# Revit family: r2018_videomax_videoserver_stoechnogo_ispolneniya
name_source: partatom
category: Устройства связи
revit_build: Autodesk Revit 2018 (Build: 20181011_1500(x64)
units: mm (PartAtom-declared; Revit-internal decimal feet)

## family parameters
Общий = Нет
Основа = Грань
При загрузке вырезать с полостями = Нет
Размер круглого соединителя = Использовать диаметр
Сохранять ориентацию аннотаций = Да
Тип детали = Нормальный
Точка расчета площади = Нет

## types (12) — shared parameters
ADSK_Версия Revit = 2018
ADSK_Версия семейства = v3
ADSK_Единица измерения = шт.
ADSK_Завод-изготовитель = ООО «Видеомакс»
ADSK_Код изделия = ТУ 26.20.15-002-37165186-2020
ADSK_Количество = 1
ADSK_Коэффициент мощности = 0.96
ADSK_Марка = VIDEOMAX-IP
ADSK_Напряжение = 230 В
ADSK_Номинальная мощность = 0 В·А
ADSK_Ток = 0 А
Material = Черный
URL = https://www.videomax-server.ru
Изготовитель = ООО «Видеомакс»
Количество интерфейсов Gigabit LAN, шт = 2
zero-valued in all types: ADSK_Масса, Количество IP-камер. шт, Количество интерфейсов 10 Gigabit LAN, шт, Максимальная мощность БП, Вт, Максимальная потребляемая мощность Вт, Максимальное тепловыделение, BTU/h, Отметка по умолчанию, Стоимость

## per-type parameters (varying)
- 19” 2U (2S): 19” 1U (1DT)=Нет; 19” 1U (1DTS)=Нет; 19” 2U (2ET)=Нет; 19” 2U (2ETS)=Нет; 19” 2U (2F)=Нет; 19” 2U (2S)=Да; 19” 3U (3ET)=Нет; 19” 3U (3ETS)=Нет; 19” 3U (3S, 3N)=Нет; 19” 4U (4A)=Нет; 19” 4U (4ET)=Нет; 19” 4U (4ETS)=Нет; ADSK_Наименование=Видеосервер стоечного исполнения 19” 2U (2S); ADSK_Обозначение=19” 2U (2S); Back=videomax_19 2U (2S) : Back; Front=videomax_19 2U (2S) : Front; Высота=88 мм; Высота в U=2; Глубина=430 мм; Изображение типоразмера=19 (2U.2S).png; Количество входов 230V, шт=1; Минимальная глубина шкафа, мм=600; Тип линейки=Standart; Указания по монтажу=Для монтажа использовать 19” салазки. Изделие комплектуется салазками SR20 либо SR26. Параметры SR20: расстояние между профилями 488 - 546 мм, габариты в сложенном состоянии 500 мм, параметры SR26: расстояние между профилями 572 - 672 мм, габариты в сложенном состоянии 650 мм.; Ширина=427 мм
- 19” 4U (4A): 19” 1U (1DT)=Нет; 19” 1U (1DTS)=Нет; 19” 2U (2ET)=Нет; 19” 2U (2ETS)=Нет; 19” 2U (2F)=Нет; 19” 2U (2S)=Нет; 19” 3U (3ET)=Нет; 19” 3U (3ETS)=Нет; 19” 3U (3S, 3N)=Нет; 19” 4U (4A)=Да; 19” 4U (4ET)=Нет; 19” 4U (4ETS)=Нет; ADSK_Наименование=Видеосервер стоечного исполнения 19” 4U (4A); ADSK_Обозначение=19” 4U (4A); Back=videomax_19 4U (4A) : Back; Front=videomax_19 4U (4A) : Front; Высота=176 мм; Высота в U=4; Глубина=450 мм; Изображение типоразмера=19 4U (4A).jpg; Количество входов 230V, шт=1; Минимальная глубина шкафа, мм=600; Тип линейки=Standart; Указания по монтажу=Для монтажа использовать комплектные 19” салазки с параметрами: расстояние между профилями 488 - 546 мм, габариты в сложенном состоянии 500 мм; Ширина=430 мм
- 19” 2U (2ET): 19” 1U (1DT)=Нет; 19” 1U (1DTS)=Нет; 19” 2U (2ET)=Да; 19” 2U (2ETS)=Нет; 19” 2U (2F)=Нет; 19” 2U (2S)=Нет; 19” 3U (3ET)=Нет; 19” 3U (3ETS)=Нет; 19” 3U (3S, 3N)=Нет; 19” 4U (4A)=Нет; 19” 4U (4ET)=Нет; 19” 4U (4ETS)=Нет; ADSK_Наименование=Видеосервер стоечного исполнения 19” 2U (2ET); ADSK_Обозначение=19” 2U (2ET); Back=videomax_19 2U (2ET) : Back; Front=videomax_19 2U (2ET) : Front; Высота=88 мм; Высота в U=2; Глубина=680 мм; Изображение типоразмера=19 (2U).png; Количество входов 230V, шт=2; Минимальная глубина шкафа, мм=1000; Тип линейки=PRO; Указания по монтажу=Для монтажа использовать комплектные 19” салазки с параметрами: расстояние между профилями 646 - 940 мм, габариты в сложенном состоянии 757 мм.; Ширина=430 мм
- 19” 2U (2ETS): 19” 1U (1DT)=Нет; 19” 1U (1DTS)=Нет; 19” 2U (2ET)=Нет; 19” 2U (2ETS)=Да; 19” 2U (2F)=Нет; 19” 2U (2S)=Нет; 19” 3U (3ET)=Нет; 19” 3U (3ETS)=Нет; 19” 3U (3S, 3N)=Нет; 19” 4U (4A)=Нет; 19” 4U (4ET)=Нет; 19” 4U (4ETS)=Нет; ADSK_Наименование=Видеосервер стоечного исполнения 19” 2U (2ETS); ADSK_Обозначение=19” 2U (2ETS); Back=videomax_19 2U (JBOD) : Back; Front=videomax_19 2U (JBOD) : Front; Высота=88 мм; Высота в U=2; Глубина=560 мм; Изображение типоразмера=19 (2U) Short.png; Количество входов 230V, шт=2; Минимальная глубина шкафа, мм=1000; Тип линейки=PRO; Указания по монтажу=Для монтажа использовать комплектные 19” салазки с параметрами: расстояние между профилями 646 - 940 мм, габариты в сложенном состоянии 757 мм.; Ширина=430 мм
- 19” 2U (2F): 19” 1U (1DT)=Нет; 19” 1U (1DTS)=Нет; 19” 2U (2ET)=Нет; 19” 2U (2ETS)=Нет; 19” 2U (2F)=Да; 19” 2U (2S)=Нет; 19” 3U (3ET)=Нет; 19” 3U (3ETS)=Нет; 19” 3U (3S, 3N)=Нет; 19” 4U (4A)=Нет; 19” 4U (4ET)=Нет; 19” 4U (4ETS)=Нет; ADSK_Наименование=Видеосервер стоечного исполнения 19” 2U (2F); ADSK_Обозначение=19” 2U (2F); Back=videomax_19 2U (2F) : Back; Front=videomax_19 2U (2F) : Front; Высота=88 мм; Высота в U=2; Глубина=686 мм; Изображение типоразмера=19 (2U.2F).png; Количество входов 230V, шт=1; Минимальная глубина шкафа, мм=1000; Тип линейки=Standart; Указания по монтажу=Для монтажа использовать комплектные 19” салазки SR26 с параметрами: расстояние между профилями 572 - 672 мм, габариты в сложенном состоянии 650 мм.; Ширина=430 мм
- 19” 3U (3ET): 19” 1U (1DT)=Нет; 19” 1U (1DTS)=Нет; 19” 2U (2ET)=Нет; 19” 2U (2ETS)=Нет; 19” 2U (2F)=Нет; 19” 2U (2S)=Нет; 19” 3U (3ET)=Да; 19” 3U (3ETS)=Нет; 19” 3U (3S, 3N)=Нет; 19” 4U (4A)=Нет; 19” 4U (4ET)=Нет; 19” 4U (4ETS)=Нет; ADSK_Наименование=Видеосервер стоечного исполнения 19” 3U (3ET); ADSK_Обозначение=19” 3U (3ET); Back=videomax_19 3U (3ET) : Back; Front=videomax_19 3U (3ET) : Front; Высота=133 мм; Высота в U=3; Глубина=680 мм; Изображение типоразмера=19 (3U).png; Количество входов 230V, шт=2; Минимальная глубина шкафа, мм=1000; Тип линейки=PRO; Указания по монтажу=Для монтажа использовать комплектные 19” салазки с параметрами: расстояние между профилями 646 - 940 мм, габариты в сложенном состоянии 757 мм.; Ширина=430 мм
- 19” 3U (3S, 3N): 19” 1U (1DT)=Нет; 19” 1U (1DTS)=Нет; 19” 2U (2ET)=Нет; 19” 2U (2ETS)=Нет; 19” 2U (2F)=Нет; 19” 2U (2S)=Нет; 19” 3U (3ET)=Нет; 19” 3U (3ETS)=Нет; 19” 3U (3S, 3N)=Да; 19” 4U (4A)=Нет; 19” 4U (4ET)=Нет; 19” 4U (4ETS)=Нет; ADSK_Наименование=Видеосервер стоечного исполнения 19” 3U (3S, 3N); ADSK_Обозначение=19” 3U (3S, 3N); Back=videomax_19 3U (3S, 3N) : Back; Front=videomax_19 3U (3S, 3N) : Front; Высота=133 мм; Высота в U=3; Глубина=530 мм; Изображение типоразмера=19 (3U.3S).png; Количество входов 230V, шт=1; Минимальная глубина шкафа, мм=800; Тип линейки=Standart; Указания по монтажу=Для монтажа использовать комплектные 19” салазки SR26 с параметрами: расстояние между профилями 572 - 672 мм, габариты в сложенном состоянии 650 мм.; Ширина=430 мм
- 19” 3U (3ETS): 19” 1U (1DT)=Нет; 19” 1U (1DTS)=Нет; 19” 2U (2ET)=Нет; 19” 2U (2ETS)=Нет; 19” 2U (2F)=Нет; 19” 2U (2S)=Нет; 19” 3U (3ET)=Нет; 19” 3U (3ETS)=Да; 19” 3U (3S, 3N)=Нет; 19” 4U (4A)=Нет; 19” 4U (4ET)=Нет; 19” 4U (4ETS)=Нет; ADSK_Наименование=Видеосервер стоечного исполнения 19” 3U (3ETS); ADSK_Обозначение=19” 3U (3ETS); Back=videomax_19 3U (JBOD) : Back; Front=videomax_19 3U (JBOD) : Front; Высота=133 мм; Высота в U=3; Глубина=560 мм; Изображение типоразмера=19 (3U) Short.png; Количество входов 230V, шт=2; Минимальная глубина шкафа, мм=1000; Тип линейки=PRO; Указания по монтажу=Для монтажа использовать комплектные 19” салазки с параметрами: расстояние между профилями 646 - 940 мм, габариты в сложенном состоянии 757 мм.; Ширина=430 мм
- 19” 4U (4ET): 19” 1U (1DT)=Нет; 19” 1U (1DTS)=Нет; 19” 2U (2ET)=Нет; 19” 2U (2ETS)=Нет; 19” 2U (2F)=Нет; 19” 2U (2S)=Нет; 19” 3U (3ET)=Нет; 19” 3U (3ETS)=Нет; 19” 3U (3S, 3N)=Нет; 19” 4U (4A)=Нет; 19” 4U (4ET)=Да; 19” 4U (4ETS)=Нет; ADSK_Наименование=Видеосервер стоечного исполнения 19” 4U (4ET); ADSK_Обозначение=19” 4U (4ET); Back=videomax_19 4U (4ET) : Back; Front=videomax_19 4U (4ET) : Front; Высота=176 мм; Высота в U=4; Глубина=680 мм; Изображение типоразмера=19 (4U).png; Количество входов 230V, шт=2; Минимальная глубина шкафа, мм=1000; Тип линейки=PRO; Указания по монтажу=Для монтажа использовать комплектные 19” салазки с параметрами: расстояние между профилями 646 - 940 мм, габариты в сложенном состоянии 757 мм.; Ширина=430 мм
- 19” 4U (4ETS): 19” 1U (1DT)=Нет; 19” 1U (1DTS)=Нет; 19” 2U (2ET)=Нет; 19” 2U (2ETS)=Нет; 19” 2U (2F)=Нет; 19” 2U (2S)=Нет; 19” 3U (3ET)=Нет; 19” 3U (3ETS)=Нет; 19” 3U (3S, 3N)=Нет; 19” 4U (4A)=Нет; 19” 4U (4ET)=Нет; 19” 4U (4ETS)=Да; ADSK_Наименование=Видеосервер стоечного исполнения 19” 4U (4ETS); ADSK_Обозначение=19” 4U (4ETS); Back=videomax_19 4U (JBOD) : Back; Front=videomax_19 4U (JBOD) : Front; Высота=176 мм; Высота в U=4; Глубина=560 мм; Изображение типоразмера=19 (4U) Short.png; Количество входов 230V, шт=2; Минимальная глубина шкафа, мм=1000; Тип линейки=PRO; Указания по монтажу=Для монтажа использовать комплектные 19” салазки с параметрами: расстояние между профилями 646 - 940 мм, габариты в сложенном состоянии 757 мм.; Ширина=429 мм
- 19” 1U (1DT): 19” 1U (1DT)=Да; 19” 1U (1DTS)=Нет; 19” 2U (2ET)=Нет; 19” 2U (2ETS)=Нет; 19” 2U (2F)=Нет; 19” 2U (2S)=Нет; 19” 3U (3ET)=Нет; 19” 3U (3ETS)=Нет; 19” 3U (3S, 3N)=Нет; 19” 4U (4A)=Нет; 19” 4U (4ET)=Нет; 19” 4U (4ETS)=Нет; ADSK_Наименование=Видеосервер стоечного исполнения 19" 1U (1DT); ADSK_Обозначение=19" 1U (1DT); Back=videomax_19pro1u : Back; Front=videomax_19pro1u : Front; Высота=44 мм; Высота в U=1; Глубина=680 мм; Изображение типоразмера=19 (1U).png; Количество входов 230V, шт=2; Минимальная глубина шкафа, мм=1000; Тип линейки=PRO; Указания по монтажу=Параметры салазок 19” в комплекте с изделием: расстояние между профилями 650 - 1050 мм, габариты в сложенном состоянии 810 мм; Ширина=438 мм
- 19” 1U (1DTS): 19” 1U (1DT)=Нет; 19” 1U (1DTS)=Да; 19” 2U (2ET)=Нет; 19” 2U (2ETS)=Нет; 19” 2U (2F)=Нет; 19” 2U (2S)=Нет; 19” 3U (3ET)=Нет; 19” 3U (3ETS)=Нет; 19” 3U (3S, 3N)=Нет; 19” 4U (4A)=Нет; 19” 4U (4ET)=Нет; 19” 4U (4ETS)=Нет; ADSK_Наименование=Видеосервер стоечного исполнения 19" 1U (1DTS); ADSK_Обозначение=19" 1U (1DTS); Back=videomax_19pro1u : Back; Front=videomax_19pro1u : Front; Высота=44 мм; Высота в U=1; Глубина=560 мм; Изображение типоразмера=19 (1U) Short.png; Количество входов 230V, шт=2; Минимальная глубина шкафа, мм=1000; Тип линейки=PRO; Указания по монтажу=Параметры салазок 19” в комплекте с изделием: расстояние между профилями 605-915 мм, габариты в сложенном состоянии 710 мм; Ширина=438 мм
